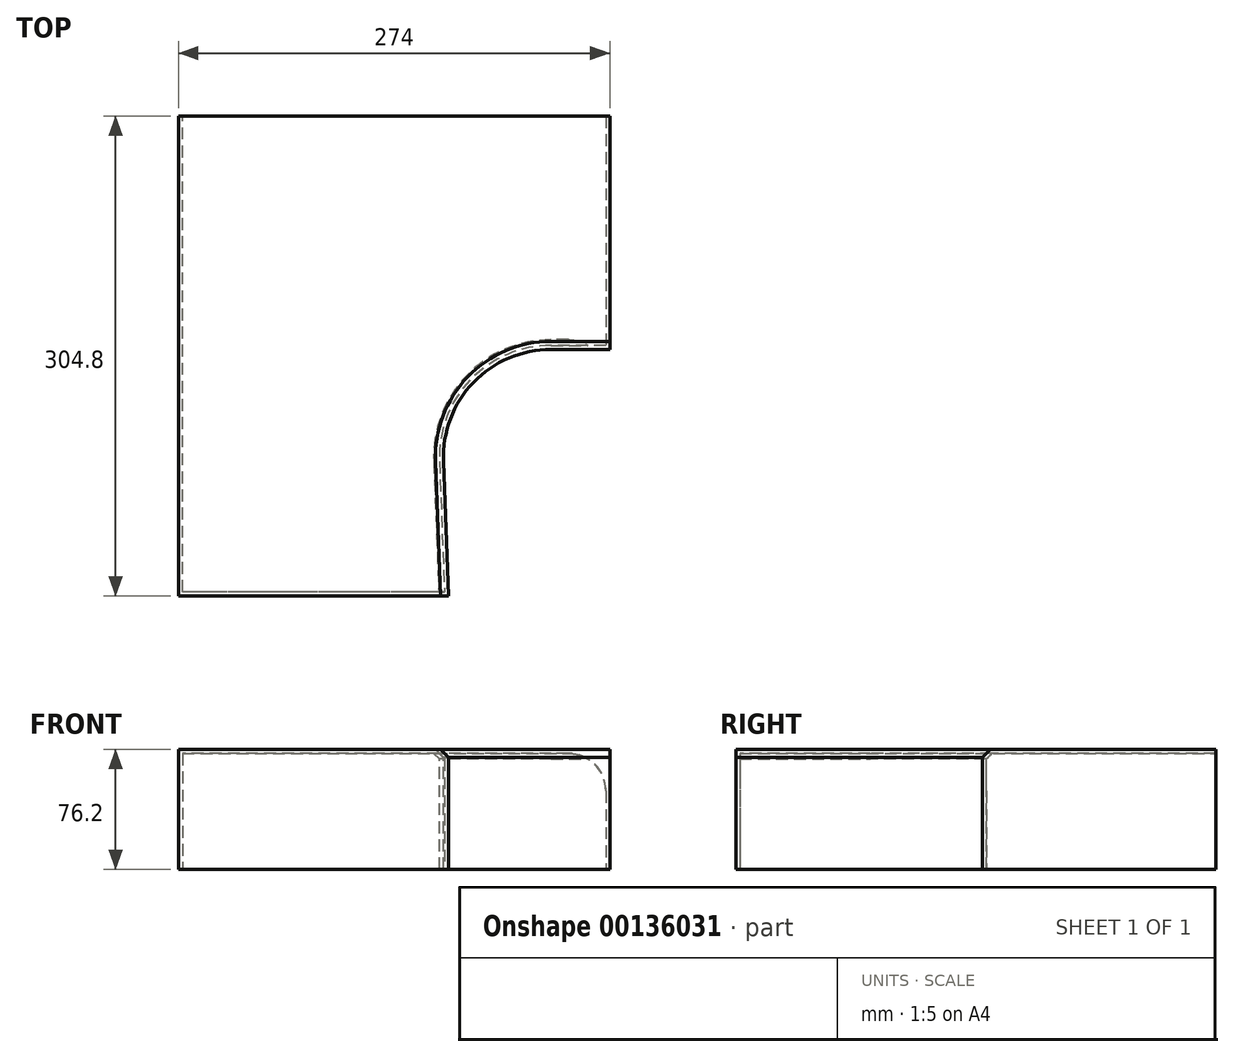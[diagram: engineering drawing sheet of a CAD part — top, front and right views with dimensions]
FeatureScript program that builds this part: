
annotation { "Feature Type Name" : "Feature", "Feature Type Description" : "" }
export const myFeature = defineFeature(function(context is Context, id is Id, definition is map)
    precondition{}
    {
        {
            var Q0;
            Q0=qCreatedBy(makeId("Top.planeOp"),FACE);
            var sketch = newSketch(context, id + "F0", { "sketchPlane" : qUnion([Q0])});
            skLineSegment(sketch, "E0", {"start": v(-147.37, -113.8) * mm, "end": v(-147.37, 191) * mm});
            skLineSegment(sketch, "E1", {"start": v(-147.37, 191) * mm, "end": v(126.63, 191) * mm});
            skLineSegment(sketch, "E2", {"start": v(126.63, 191) * mm, "end": v(126.63, 42.81) * mm});
            skLineSegment(sketch, "E3", {"start": v(126.63, 42.81) * mm, "end": v(18.15, 42.81) * mm});
            skLineSegment(sketch, "E4", {"start": v(18.15, 42.81) * mm, "end": v(24.25, -113.8) * mm});
            skLineSegment(sketch, "E5", {"start": v(24.25, -113.8) * mm, "end": v(-147.37, -113.8) * mm});
            skSolve(sketch);
        }
        {
            var Q0;
            Q0=makeQuery(id+"F0.imprint","IMPRINT",FACE,{"disambiguationData":[TD([[makeQuery(id+"F0.imprint","IMPRINT",EDGE,{"derivedFrom":sQuery(id+"F0.wireOp",EDGE,"E0")}),-1.0]])]});
            extrude(context, id + "F1", {"entities" : qUnion([Q0]), "depth" : 76.2 * mm});
        }
        {
            var Q0;
            Q0=makeQuery(id+"F1.opExtrude","SWEPT_EDGE",EDGE,{"disambiguationData":[OSD([sQuery(id+"F0.wireOp",EDGE,"E3"),sQuery(id+"F0.wireOp",EDGE,"E4")])]});
            fillet(context, id + "F2", {"entities" : qUnion([Q0]), "radius" : 68.46 * mm, "tangentPropagation" : true, "allowEdgeOverflow" : false});
        }
        {
            var Q0;
            Q0=makeQuery(id+"F1.opExtrude","CAP_EDGE",EDGE,{"disambiguationData":[OSD([sQuery(id+"F0.wireOp",EDGE,"E4")])],"isStart":false});
            chamfer(context, id + "F3", {"entities" : qUnion([Q0]), "width" : 5.08 * mm, "tangentPropagation" : true});
        }
        {
            var Q0;
            Q0=makeQuery(id+"F1.opExtrude","CAP_FACE",FACE,{"disambiguationData":[OSD([sQuery(id+"F0.wireOp",EDGE,"E0"),sQuery(id+"F0.wireOp",EDGE,"E1"),sQuery(id+"F0.wireOp",EDGE,"E2"),sQuery(id+"F0.wireOp",EDGE,"E3"),sQuery(id+"F0.wireOp",EDGE,"E4"),sQuery(id+"F0.wireOp",EDGE,"E5")])],"isStart":true});
            var Q1;
            Q1=makeQuery(id+"F1.opExtrude","SWEPT_FACE",FACE,{"disambiguationData":[OSD([sQuery(id+"F0.wireOp",EDGE,"E1")])]});
            shell(context, id + "F4", {"entities" : qUnion([Q0, Q1]), "thickness" : 2.54 * mm});
        }
        {
            var Q0;
            {var subQ0=sQuery(id+"F0.wireOp",EDGE,"E2");Q0=makeQuery(id+"F4.opShell","OFFSET_EDGE",EDGE,{"disambiguationData":[OSD([subQ0]),TDD([makeQuery(id+"F1.opExtrude","CAP_EDGE",EDGE,{"disambiguationData":[OSD([subQ0])],"isStart":false})])]});}
            fillet(context, id + "F5", {"entities" : qUnion([Q0]), "radius" : 23.9 * mm, "tangentPropagation" : true, "allowEdgeOverflow" : false});
        }
    });
